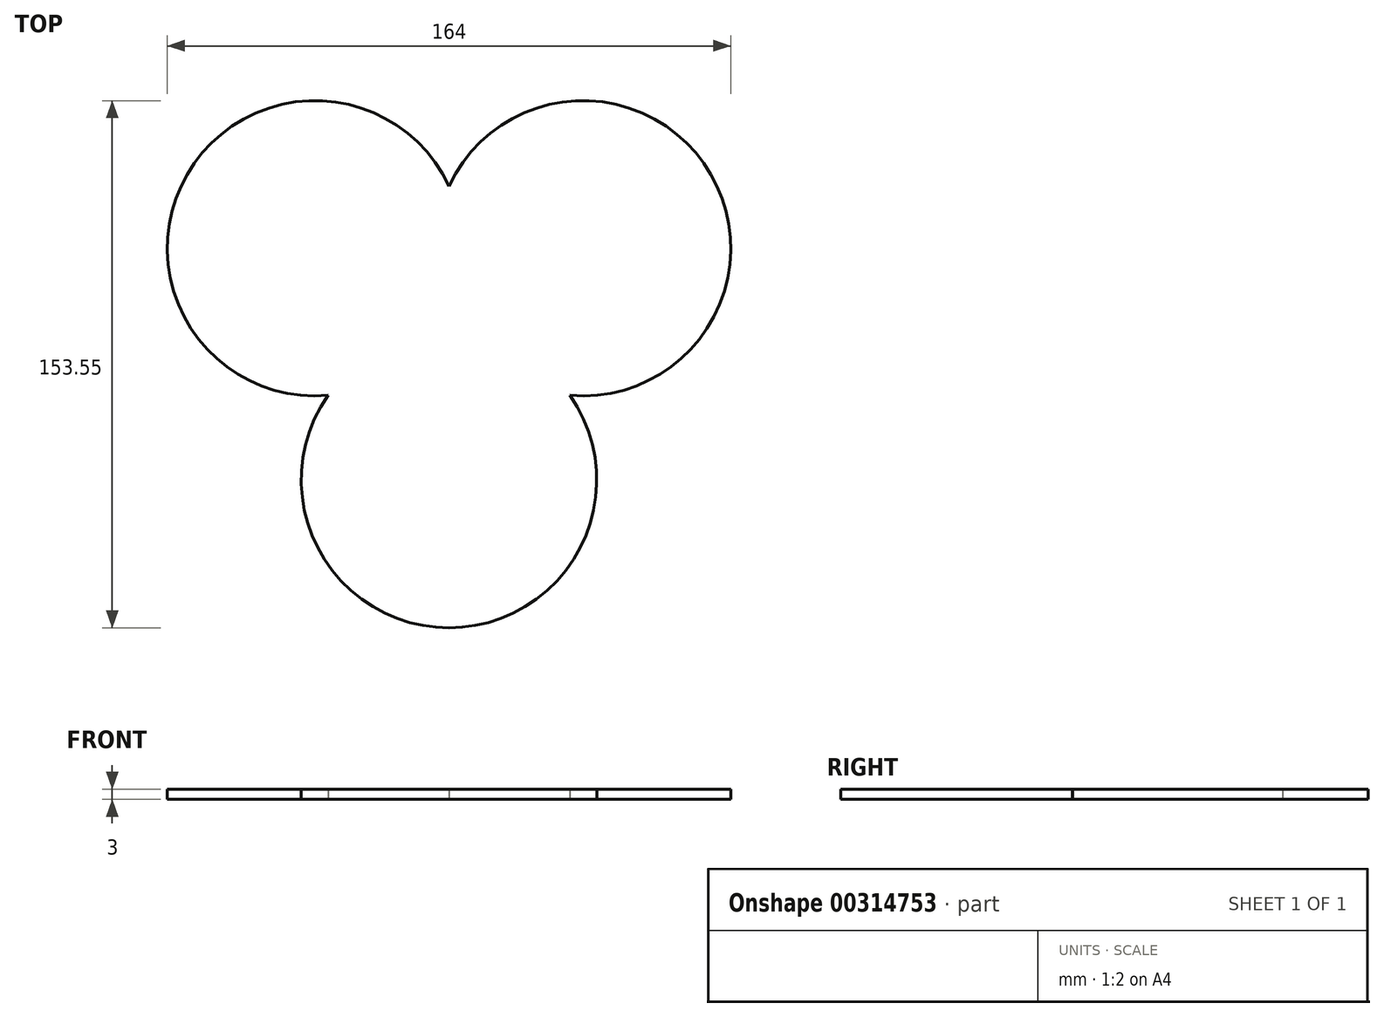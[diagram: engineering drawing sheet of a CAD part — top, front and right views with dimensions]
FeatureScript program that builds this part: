
annotation { "Feature Type Name" : "Feature", "Feature Type Description" : "" }
export const myFeature = defineFeature(function(context is Context, id is Id, definition is map)
    precondition{}
    {
        {
            var Q0;
            Q0=qCreatedBy(makeId("Top.planeOp"),FACE);
            var sketch = newSketch(context, id + "F0", { "sketchPlane" : qUnion([Q0])});
            skCircle(sketch, "E0.cCircle", {"center": v(0, 0) * mm, "radius": 22.52 * mm, "construction": true});
            skLineSegment(sketch, "E0.0", {"start": v(-39, 22.52) * mm, "end": v(39, 22.52) * mm, "construction": true});
            skLineSegment(sketch, "E0.1", {"start": v(39, 22.52) * mm, "end": v(0, -45.03) * mm, "construction": true});
            skLineSegment(sketch, "E0.2", {"start": v(0, -45.03) * mm, "end": v(-39, 22.52) * mm, "construction": true});
            skPoint(sketch, "E0.0.midPoint", {"position": v(0, 22.52) * mm});
            skArc(sketch, "E1", {"start": v(-1, 22.52) * mm, "mid": v(-1, 22.5) * mm, "end": v(-1, 22.5) * mm});
            skArc(sketch, "E2", {"start": v(-19.98, -10.38) * mm, "mid": v(-20, -10.39) * mm, "end": v(-20, -10.4) * mm});
            skArc(sketch, "E3.trimOffspring", {"start": v(1, 22.5) * mm, "mid": v(1, 22.5) * mm, "end": v(1, 22.52) * mm});
            skArc(sketch, "E4.trimOffspring", {"start": v(18.98, -12.11) * mm, "mid": v(19, -12.12) * mm, "end": v(19, -12.12) * mm});
            skArc(sketch, "E5.trimOffspring", {"start": v(20, -10.4) * mm, "mid": v(20, -10.39) * mm, "end": v(19.98, -10.38) * mm});
            skArc(sketch, "E6.trimOffspring", {"start": v(-19, -12.12) * mm, "mid": v(-19, -12.12) * mm, "end": v(-18.98, -12.11) * mm});
            skArc(sketch, "E7.0", {"start": v(0, 40.63) * mm, "mid": v(-76.24, 44.02) * mm, "end": v(-35.18, -20.31) * mm});
            skArc(sketch, "E7.1", {"start": v(35.18, -20.31) * mm, "mid": v(76.24, 44.02) * mm, "end": v(0, 40.63) * mm});
            skArc(sketch, "E7.2", {"start": v(-35.18, -20.31) * mm, "mid": v(0, -88.03) * mm, "end": v(35.18, -20.31) * mm});
            skSolve(sketch);
        }
        {
            var Q0;
            Q0=makeQuery(id+"F0.imprint","IMPRINT",FACE,{"disambiguationData":[TD([[makeQuery(id+"F0.imprint","IMPRINT",EDGE,{"derivedFrom":sQuery(id+"F0.wireOp",EDGE,"E7.0")}),1.0]])]});
            extrude(context, id + "F1", {"entities" : qUnion([Q0]), "depth" : 3 * mm});
        }
    });
